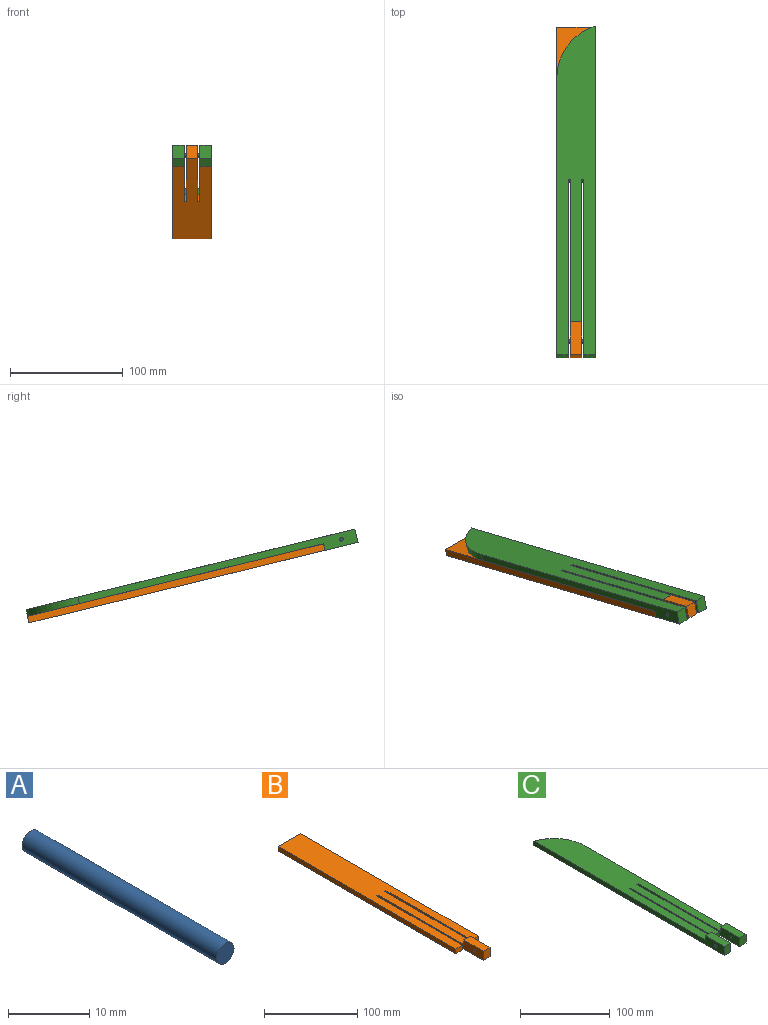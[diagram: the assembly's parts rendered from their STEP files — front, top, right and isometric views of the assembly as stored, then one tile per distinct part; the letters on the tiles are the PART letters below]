
ASSEMBLY  parts=3 mates=3
PART A: 3 faces, bbox 3x34x3 mm
  f0: cylinder r=1.5mm len=34mm, axis (0,1,0), area 320.4mm2, adj f1,f2
  f1: plane 3x3mm, normal (0,-1,0), area 7.1mm2, adj f0
  f2: plane 3x3mm, normal (0,1,0), area 7.1mm2, adj f0
PART B: 17 faces, bbox 34x300x12 mm
  f0: plane 270x34mm, normal (0,0,1), area 8660mm2, adj f1,f3,f4,f5,f6,f7,f8,f9
  f1: plane 160x12mm, normal (-1,0,0), area 1132.9mm2, adj f0,f2,f12,f13,f14,f15,f16
  f2: plane 12x10mm, normal (0,-1,0), area 120mm2, adj f1,f3,f13,f15
  f3: plane 160x12mm, normal (1,0,0), area 1132.9mm2, adj f0,f2,f4,f13,f14,f15,f16
  f4: plane 6x2mm, normal (0,-1,0), area 12mm2, adj f0,f3,f5,f13
  f5: plane 130x6mm, normal (-1,0,0), area 780mm2, adj f0,f4,f6,f13
  f6: plane 10x6mm, normal (0,-1,0), area 60mm2, adj f0,f5,f7,f13
  f7: plane 270x6mm, normal (1,0,0), area 1620mm2, adj f0,f6,f8,f13
  f8: plane 34x6mm, normal (0,1,0), area 204mm2, adj f0,f7,f9,f13
  f9: plane 270x6mm, normal (-1,0,0), area 1620mm2, adj f0,f8,f10,f13
  f10: plane 10x6mm, normal (0,-1,0), area 60mm2, adj f0,f9,f11,f13
  f11: plane 130x6mm, normal (1,0,0), area 780mm2, adj f0,f10,f12,f13
  f12: plane 6x2mm, normal (0,-1,0), area 12mm2, adj f0,f1,f11,f13
  f13: plane 300x34mm, normal (0,0,-1), area 8960mm2, adj f1,f2,f3,f4,f5,f6,f7,f8
  f14: plane 10x6mm, normal (0,1,0), area 60mm2, adj f0,f1,f3,f15
  f15: plane 30x10mm, normal (0,0,1), area 300mm2, adj f1,f2,f3,f14
  f16: cylinder r=1.5mm len=10mm, axis (-1,0,0), area 94.2mm2, adj f1,f3
PART C: 20 faces, bbox 34x300x12 mm
  f0: plane 270x34mm, normal (0,0,1), area 8226.8mm2, adj f1,f2,f3,f4,f5,f6,f7,f9
  f1: plane 160x12mm, normal (1,0,0), area 1132.9mm2, adj f0,f2,f11,f12,f13,f14,f18
  f2: plane 6x2mm, normal (0,-1,0), area 12mm2, adj f0,f1,f3,f12
  f3: plane 130x6mm, normal (-1,0,0), area 780mm2, adj f0,f2,f4,f12
  f4: plane 10x6mm, normal (0,-1,0), area 60mm2, adj f0,f3,f5,f12
  f5: plane 130x6mm, normal (1,0,0), area 780mm2, adj f0,f4,f6,f12
  f6: plane 6x2mm, normal (0,-1,0), area 12mm2, adj f0,f5,f7,f12
  f7: plane 160x12mm, normal (-1,0,0), area 1132.9mm2, adj f0,f6,f8,f12,f15,f16,f17
  f8: plane 12x10mm, normal (0,-1,0), area 120mm2, adj f7,f9,f12,f16
  f9: plane 252.63x12mm, normal (1,0,0), area 1688.7mm2, adj f0,f8,f12,f15,f16,f17,f19
  f10: plane 300x12mm, normal (-1,0,0), area 1972.9mm2, adj f0,f11,f12,f13,f14,f18,f19
  f11: plane 12x10mm, normal (0,-1,0), area 120mm2, adj f1,f10,f12,f14
  f12: plane 300x34mm, normal (0,0,-1), area 8826.8mm2, adj f1,f2,f3,f4,f5,f6,f7,f8
  f13: plane 10x6mm, normal (0,1,0), area 60mm2, adj f0,f1,f10,f14
  f14: plane 30x10mm, normal (0,0,1), area 300mm2, adj f1,f10,f11,f13
  f15: plane 10x6mm, normal (0,1,0), area 60mm2, adj f0,f7,f9,f16
  f16: plane 30x10mm, normal (0,0,1), area 300mm2, adj f7,f8,f9,f15
  f17: cylinder r=1.5mm len=10mm, axis (-1,0,0), area 94.2mm2, adj f7,f9
  f18: cylinder r=1.5mm len=10mm, axis (-1,0,0), area 94.2mm2, adj f1,f10
  f19: cylinder r=50mm len=47.37mm, axis (0,0,-1), area 373.5mm2, adj f0,f9,f10,f12
PLACE A rot(axis=(0.71,0.71,0),180deg) t=(-91.34,-142.05,158.06)mm fixed
PLACE B rot(axis=(-1,0,0),13.8deg) t=(-89.25,-86.17,138.41)mm
PLACE C rot(axis=(0,0.99,-0.12),180deg) t=(-91.34,-8.24,131.63)mm
MATE revolute C.f17 <-> A.f0  axis (1,0,0) through (-74.34,-142.05,158.28)mm
MATE cylindrical A.f0 <-> C.f17  axis (1,0,0) through (-74.34,-142.05,158.28)mm
MATE revolute B.f16 <-> A.f0  axis (-1,0,0) through (-86.34,-142.05,158.28)mm
